# Revit family: isabella_mirror
name_source: partatom
category: Furniture Systems
units: mm (PartAtom-declared; Revit-internal decimal feet)

## family parameters
Always vertical = No
Cut with Voids When Loaded = No
Part Type = Normal
Room Calculation Point = No
Round Connector Dimension = Use Diameter
Shared = No
Work Plane-Based = No

## types (1)
- Default
    BIMobject category = Mirrors
    BOSUseNativeGeometries = 1
    Brand url = http://www.dahl.se
    Default Elevation = 0' - 0"
    Design country = Sweden
    EAN code = https://7332508044075
    Edition number = 1
    IFC Classification = Furnishing Element
    Manufacturer country = Poland
    Manufacturer name = Alterna
    Masterformat 2014 Code = 08 83 00
    Masterformat 2014 Description = Mirrors
    Material main = Glass
    Material secondary = Particleboard
    Nominal height = 700
    Nominal width = 400
    Product Guid = 0e8bea60-3921-46eb-8f61-36048dad2c40
    Product SKU = Isabellaspegel
    Product data url = https://bimobject.com
    Product family = Sanitet
    Product group = Badrumsm??bler
    Product name = Isabella Mirror
    Product url = http://www.rskdatabasen.se
    QR code = http://bimobject.com
    UNSPSC Code = 56
    Weight Net (Kg) = 0

## geometry (parser evidence)
native form markers: Sweep x3
no freeform markers — native parametric forms only
